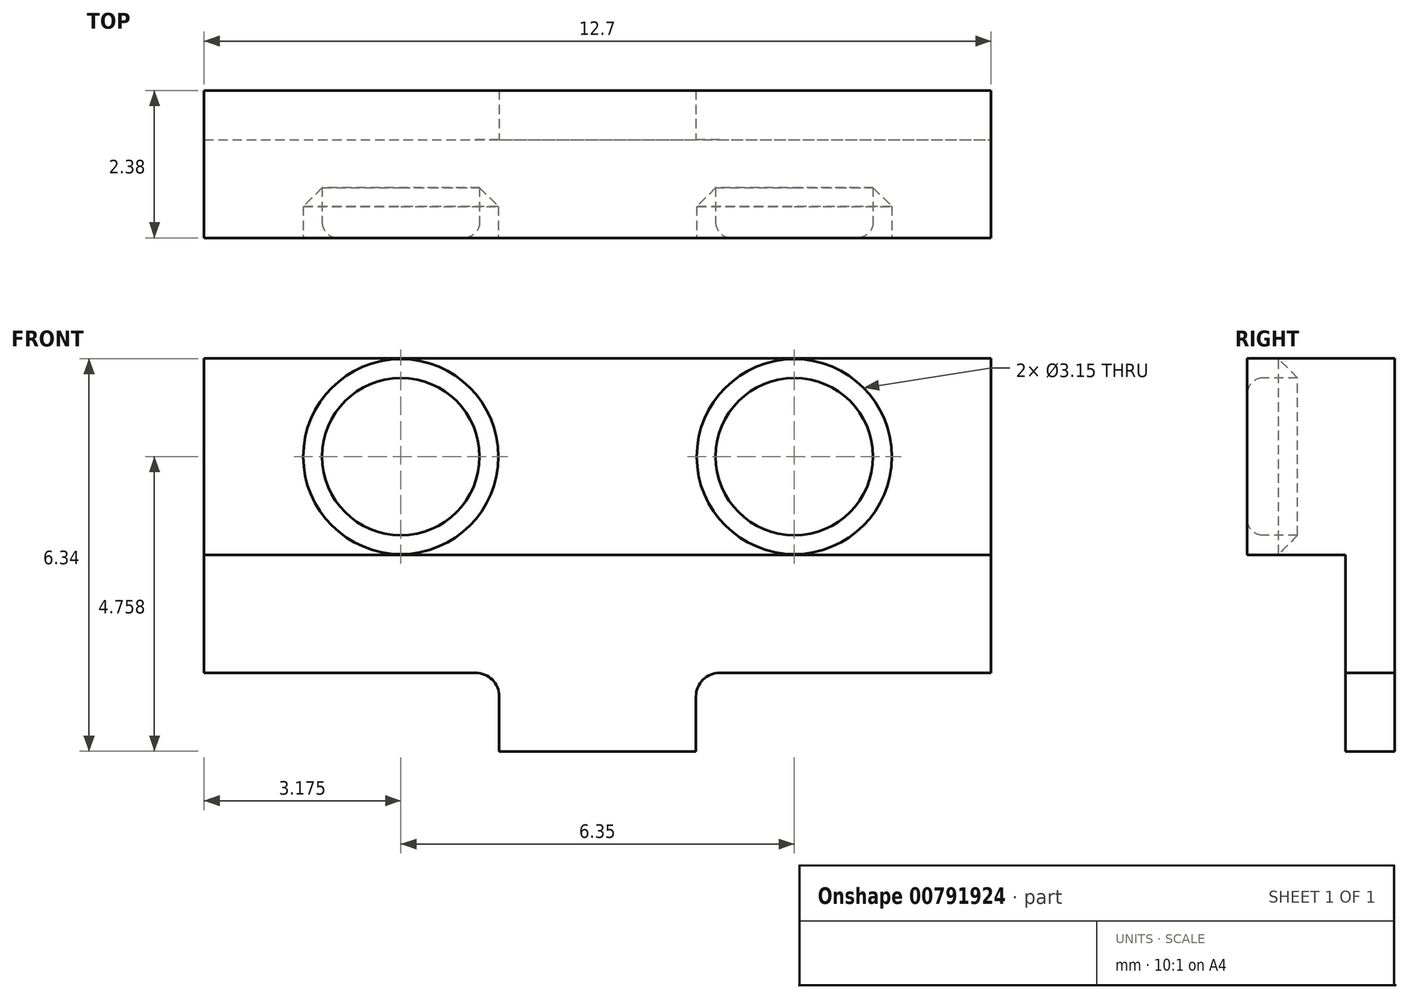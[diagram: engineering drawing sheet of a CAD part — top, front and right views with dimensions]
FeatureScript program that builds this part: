
annotation { "Feature Type Name" : "Feature", "Feature Type Description" : "" }
export const myFeature = defineFeature(function(context is Context, id is Id, definition is map)
    precondition{}
    {
        {
            var Q0;
            Q0=qCreatedBy(makeId("Front.planeOp"),FACE);
            var sketch = newSketch(context, id + "F0", { "sketchPlane" : qUnion([Q0])});
            skLineSegment(sketch, "E0.bottom", {"start": v(-6.35, 3.18) * mm, "end": v(6.35, 3.18) * mm});
            skLineSegment(sketch, "E0.top", {"start": v(-6.35, -3.18) * mm, "end": v(6.35, -3.18) * mm});
            skLineSegment(sketch, "E0.left", {"start": v(-6.35, 3.18) * mm, "end": v(-6.35, -3.18) * mm});
            skLineSegment(sketch, "E0.right", {"start": v(6.35, 3.18) * mm, "end": v(6.35, -3.18) * mm});
            skSolve(sketch);
        }
        {
            var Q0;
            Q0=makeQuery(id+"F0.imprint","IMPRINT",FACE,{"disambiguationData":[TD([[makeQuery(id+"F0.imprint","IMPRINT",EDGE,{"derivedFrom":sQuery(id+"F0.wireOp",EDGE,"E0.bottom")}),-1.0]])]});
            extrude(context, id + "F1", {"entities" : qUnion([Q0]), "depth" : 0.8 * mm, "offsetDistance" : 25.4 * mm});
        }
        {
            var Q0;
            Q0=makeQuery(id+"F1.opExtrude","CAP_FACE",FACE,{"disambiguationData":[OSD([sQuery(id+"F0.wireOp",EDGE,"E0.bottom"),sQuery(id+"F0.wireOp",EDGE,"E0.top"),sQuery(id+"F0.wireOp",EDGE,"E0.left"),sQuery(id+"F0.wireOp",EDGE,"E0.right")])],"isStart":false});
            var sketch = newSketch(context, id + "F2", { "sketchPlane" : qUnion([Q0])});
            skLineSegment(sketch, "E1", {"start": v(-6.35, 0) * mm, "end": v(6.35, 0) * mm});
            skLineSegment(sketch, "E2", {"start": v(-6.35, -1.9) * mm, "end": v(-1.59, -1.9) * mm});
            skLineSegment(sketch, "E3", {"start": v(-1.59, -1.9) * mm, "end": v(-1.59, -3.18) * mm});
            skLineSegment(sketch, "E4", {"start": v(1.59, -3.18) * mm, "end": v(1.59, -1.9) * mm});
            skLineSegment(sketch, "E5", {"start": v(1.59, -1.9) * mm, "end": v(6.35, -1.9) * mm});
            skSolve(sketch);
        }
        {
            var Q0;
            {var subQ0=sQuery(id+"F2.wireOp",EDGE,"E2");Q0=makeQuery(id+"F2.imprint","IMPRINT",FACE,{"disambiguationData":[TD([[makeQuery(id+"F2.imprint","IMPRINT",EDGE,{"derivedFrom":subQ0}),-1.0]])]});}
            var Q1;
            {var subQ0=sQuery(id+"F2.wireOp",EDGE,"E4");Q1=makeQuery(id+"F2.imprint","IMPRINT",FACE,{"disambiguationData":[TD([[makeQuery(id+"F2.imprint","IMPRINT",EDGE,{"derivedFrom":subQ0}),-1.0]])]});}
            extrude(context, id + "F3", {"entities" : qUnion([Q0, Q1]), "operationType" : NewBodyOperationType.REMOVE, "oppositeDirection" : true, "depth" : 25.4 * mm, "offsetDistance" : 25.4 * mm});
        }
        {
            var Q0;
            Q0=makeQuery(id+"F3.boolean.opBoolean","COPY",EDGE,{"derivedFrom":makeQuery(id+"F3.opExtrude","SWEPT_EDGE",EDGE,{"disambiguationData":[OSD([sQuery(id+"F0.wireOp",EDGE,"E0.top"),sQuery(id+"F2.wireOp",EDGE,"E3")])]})});
            var Q1;
            Q1=makeQuery(id+"F3.boolean.opBoolean","COPY",EDGE,{"derivedFrom":makeQuery(id+"F3.opExtrude","SWEPT_EDGE",EDGE,{"disambiguationData":[OSD([sQuery(id+"F0.wireOp",EDGE,"E0.top"),sQuery(id+"F2.wireOp",EDGE,"E4")])]})});
            var Q2;
            Q2=makeQuery(id+"F3.boolean.opBoolean","COPY",EDGE,{"derivedFrom":makeQuery(id+"F3.opExtrude","SWEPT_EDGE",EDGE,{"disambiguationData":[OSD([sQuery(id+"F0.wireOp",EDGE,"E0.left"),sQuery(id+"F2.wireOp",EDGE,"E2")])]})});
            var Q3;
            Q3=makeQuery(id+"F3.boolean.opBoolean","COPY",EDGE,{"derivedFrom":makeQuery(id+"F3.opExtrude","SWEPT_EDGE",EDGE,{"disambiguationData":[OSD([sQuery(id+"F0.wireOp",EDGE,"E0.right"),sQuery(id+"F2.wireOp",EDGE,"E5")])]})});
            var Q4;
            Q4=makeQuery(id+"F3.boolean.opBoolean","COPY",EDGE,{"derivedFrom":makeQuery(id+"F3.opExtrude","SWEPT_EDGE",EDGE,{"disambiguationData":[OSD([sQuery(id+"F2.wireOp",EDGE,"E4"),sQuery(id+"F2.wireOp",EDGE,"E5")])]})});
            var Q5;
            Q5=makeQuery(id+"F3.boolean.opBoolean","COPY",EDGE,{"derivedFrom":makeQuery(id+"F3.opExtrude","SWEPT_EDGE",EDGE,{"disambiguationData":[OSD([sQuery(id+"F2.wireOp",EDGE,"E2"),sQuery(id+"F2.wireOp",EDGE,"E3")])]})});
            fillet(context, id + "F4", {"entities" : qUnion([Q0, Q1, Q2, Q3, Q4, Q5]), "radius" : 0.38 * mm, "tangentPropagation" : true, "allowEdgeOverflow" : false});
        }
        {
            var Q0;
            {var subQ0=sQuery(id+"F2.wireOp",EDGE,"E1");Q0=makeQuery(id+"F2.imprint","IMPRINT",FACE,{"disambiguationData":[TD([[makeQuery(id+"F2.imprint","IMPRINT",EDGE,{"derivedFrom":subQ0}),1.0]])]});}
            extrude(context, id + "F5", {"entities" : qUnion([Q0]), "operationType" : NewBodyOperationType.ADD, "depth" : 1.59 * mm, "offsetDistance" : 25.4 * mm});
        }
        {
            var Q0;
            Q0=makeQuery(id+"F5.opExtrude","CAP_FACE",FACE,{"disambiguationData":[OSD([sQuery(id+"F0.wireOp",EDGE,"E0.bottom"),sQuery(id+"F0.wireOp",EDGE,"E0.left"),sQuery(id+"F0.wireOp",EDGE,"E0.right"),sQuery(id+"F2.wireOp",EDGE,"E1")])],"isStart":false});
            var sketch = newSketch(context, id + "F6", { "sketchPlane" : qUnion([Q0])});
            skLineSegment(sketch, "E6", {"start": v(0, 3.18) * mm, "end": v(0, 0) * mm, "construction": true});
            skLineSegment(sketch, "E7", {"start": v(0, 0) * mm, "end": v(-6.35, 0) * mm});
            skLineSegment(sketch, "E8", {"start": v(-6.35, 0) * mm, "end": v(-6.35, 3.18) * mm});
            skLineSegment(sketch, "E9", {"start": v(-6.35, 3.18) * mm, "end": v(0, 3.18) * mm});
            skLineSegment(sketch, "E10", {"start": v(0, 3.18) * mm, "end": v(6.35, 3.18) * mm});
            skLineSegment(sketch, "E11", {"start": v(6.35, 3.18) * mm, "end": v(6.35, 0) * mm});
            skLineSegment(sketch, "E12", {"start": v(6.35, 0) * mm, "end": v(0, 0) * mm});
            skLineSegment(sketch, "E13", {"start": v(-3.18, 0) * mm, "end": v(-3.18, 3.18) * mm, "construction": true});
            skLineSegment(sketch, "E14", {"start": v(3.18, 3.18) * mm, "end": v(3.17, 0) * mm, "construction": true});
            skCircle(sketch, "E15", {"center": v(-3.18, 1.59) * mm, "radius": 1.57 * mm});
            skCircle(sketch, "E16", {"center": v(3.18, 1.59) * mm, "radius": 1.57 * mm});
            skCircle(sketch, "E17", {"center": v(-3.18, 1.59) * mm, "radius": 1.27 * mm});
            skCircle(sketch, "E18", {"center": v(3.18, 1.59) * mm, "radius": 1.27 * mm});
            skSolve(sketch);
        }
        {
            var Q0;
            Q0=makeQuery(id+"F6.imprint","IMPRINT",FACE,{"disambiguationData":[TD([[makeQuery(id+"F6.imprint","IMPRINT",EDGE,{"derivedFrom":sQuery(id+"F6.wireOp",EDGE,"E15")}),1.0]])]});
            var Q1;
            Q1=makeQuery(id+"F6.imprint","IMPRINT",FACE,{"disambiguationData":[TD([[makeQuery(id+"F6.imprint","IMPRINT",EDGE,{"derivedFrom":sQuery(id+"F6.wireOp",EDGE,"E16")}),1.0]])]});
            extrude(context, id + "F7", {"entities" : qUnion([Q0, Q1]), "operationType" : NewBodyOperationType.REMOVE, "oppositeDirection" : true, "depth" : 0.89 * mm, "offsetDistance" : 25.4 * mm});
        }
        {
            var Q0;
            Q0=makeQuery(id+"F7.boolean.opBoolean","COPY",EDGE,{"derivedFrom":makeQuery(id+"F7.opExtrude","CAP_EDGE",EDGE,{"disambiguationData":[OSD([sQuery(id+"F6.wireOp",EDGE,"E15")])],"isStart":false})});
            var Q1;
            Q1=makeQuery(id+"F7.boolean.opBoolean","COPY",EDGE,{"derivedFrom":makeQuery(id+"F7.opExtrude","CAP_EDGE",EDGE,{"disambiguationData":[OSD([sQuery(id+"F6.wireOp",EDGE,"E16")])],"isStart":false})});
            chamfer(context, id + "F8", {"entities" : qUnion([Q0, Q1]), "width" : 0.38 * mm, "tangentPropagation" : true});
        }
        {
            var Q0;
            Q0=makeQuery(id+"F7.boolean.opBoolean","COPY",EDGE,{"derivedFrom":makeQuery(id+"F7.opExtrude","CAP_EDGE",EDGE,{"disambiguationData":[OSD([sQuery(id+"F6.wireOp",EDGE,"E17")])],"isStart":true})});
            var Q1;
            Q1=makeQuery(id+"F7.boolean.opBoolean","COPY",EDGE,{"derivedFrom":makeQuery(id+"F7.opExtrude","CAP_EDGE",EDGE,{"disambiguationData":[OSD([sQuery(id+"F6.wireOp",EDGE,"E18")])],"isStart":true})});
            fillet(context, id + "F9", {"entities" : qUnion([Q0, Q1]), "radius" : 0.25 * mm, "tangentPropagation" : true, "allowEdgeOverflow" : false});
        }
    });
